# Revit family: Sanitary_Taps-Mixers_DURAVIT-AG_A-1-Single-lever-washbasin-mixer A11040__77
name_source: partatom
category: Plumbing Fixtures
revit_build: Autodesk Revit 2018 (Build: 20170223_1515(x64)
units: mm (PartAtom-declared; Revit-internal decimal feet)

## family parameters
Always vertical = No
Cut with Voids When Loaded = No
OmniClass Number = 23.31.11.00
OmniClass Title = Faucets
Part Type = Normal
Room Calculation Point = No
Round Connector Dimension = Use Diameter
Shared = No
Work Plane-Based = Yes

## types (2) — shared parameters
Always visible = Yes
Connector Description = Water Inlet 9.5 mm
Default Elevation = 1219.2 mm  [stored 4 ft]
Depth = 43 mm  [stored 0.141076 ft]
Description = Duravit A.1 Single lever washbasin mixer Chrome High Gloss 222x43x295 mm - A11040001010 Duravit A.1 Single lever washbasin mixer Chrome High Gloss 222x43x295 mm - A11040002010
Diameter = 9.53 mm
Edition number = 1
Height = 295 mm  [stored 0.967848 ft]
IFC Classification = Valve
Installation instructions = http://pro.duravit.com
Manufacturer = Duravit
Manufacturer name = DURAVIT AG
Masterformat 2014 Code = 22 41 39
Masterformat 2014 Description = Residential Faucets, Supplies, and Trim
Material 1 = Duravit - Metal - 10 - Chrome
Material main = Chrome
Model = A.1 Single lever washbasin mixer 222x43x295 mm - A11040
OmniClass Code = 23-31 11 00
OmniClass Description = Faucets
Product Guid = 2423577e-e0b6-416a-b42a-7c7518f9402b
Product SKU = A1-Single-lever-washbasin-mixer-222x43x295-mm-A11040
Product certification = http://pro.duravit.com
Product data url = https://bimobject.com
Product name = A.1 Single lever washbasin mixer 222x43x295 mm - A11040
Product url = http://pro.duravit.com
QR code = https://bimobject.com
Technical description = http://pro.duravit.com
UNSPSC Code = 301815
URL = http://pro.duravit.com
Uniclass 2015 Code = Pr_40_20_87_98
Uniclass 2015 Name = Washbasin taps
Uniformat II Code = D2010
Uniformat II Description = Plumbing Fixtures
Weight = 2.0 kg
Width = 222 mm
Youtube clip = http://pro.duravit.com

## per-type parameters (varying)
| type | Pop up waste option - On |
| A.1 Single lever washbasin mixer without pop-up waste - A11040002010 | No |
| A.1 Single lever washbasin mixer with pop-up waste - A11040001010 | Yes |

note: [stored X ft] marks values corroborated as IEEE doubles in the binary element streams (Revit-internal decimal feet)

## geometry (parser evidence)
native form markers: Sweep x4
no freeform markers — native parametric forms only
